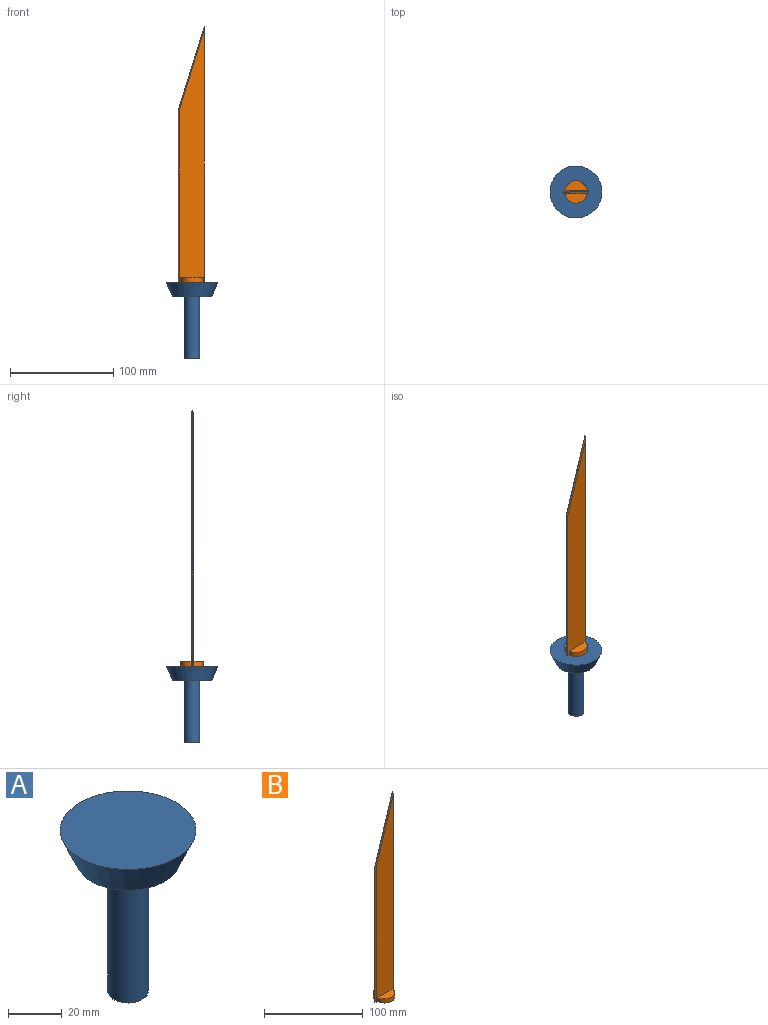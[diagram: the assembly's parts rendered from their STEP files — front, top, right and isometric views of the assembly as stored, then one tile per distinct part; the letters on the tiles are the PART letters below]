
ASSEMBLY  parts=2 mates=1
PART A: 5 faces, bbox 50.4x50.4x73.2 mm
  f0: plane 50.44x50.44mm, normal (0,0,1), area 1998.6mm2, adj f1
  f1: cone r=25.22mm half-angle=23.7deg, axis (0,0,1), area 2088mm2, adj f0,f2
  f2: plane 38.42x38.42mm, normal (0,0,-1), area 981.7mm2, adj f1,f3
  f3: cylinder r=7.52mm len=59.46mm, axis (0,0,1), area 2808.4mm2, adj f2,f4
  f4: plane 15.03x15.03mm, normal (0,0,-1), area 177.5mm2, adj f3
PART B: 13 faces, bbox 25.4x21.8x248.8 mm
  f0: plane 2.61x2mm, normal (0,0,-1), area 4.1mm2, adj f1,f2,f7,f8,f10
  f1: plane 245.33x24.4mm, normal (0,-1,0), area 4918.2mm2, adj f0,f3,f4,f5,f7,f10,f11
  f2: plane 245.33x24.4mm, normal (0,1,0), area 4917.6mm2, adj f0,f3,f4,f6,f8,f9,f10
  f3: plane 2x1.14mm, normal (0,0,-1), area 2.2mm2, adj f1,f2,f4,f10
  f4: plane 248.71x2mm, normal (1,0,0), area 494mm2, adj f1,f2,f3,f5,f6
  f5: plane 82.19x25.4mm, normal (-0.68,-0.71,0.21), area 119.1mm2, adj f1,f4,f6,f7
  f6: plane 82.19x25.4mm, normal (-0.68,0.71,0.21), area 119.1mm2, adj f2,f4,f5,f8
  f7: plane 166.66x1mm, normal (-0.71,-0.71,0), area 235.6mm2, adj f0,f1,f5,f8
  f8: plane 166.66x1mm, normal (-0.71,0.71,0), area 235.6mm2, adj f0,f2,f6,f7
  f9: plane 21.77x10.24mm, normal (0,0,1), area 172.3mm2, adj f2,f10
  f10: cylinder r=10.91mm len=21.81mm, axis (0,0,-1), area 323mm2, adj f0,f1,f2,f3,f9,f11,f12
  f11: plane 21.65x9.58mm, normal (0,0,1), area 157.9mm2, adj f1,f10
  f12: plane 21.81x21.81mm, normal (0,0,-1), area 373.8mm2, adj f10
PLACE A t=(93.8,114.69,15.5)mm
PLACE B t=(80.27,115.36,135.11)mm
MATE fastened B.f10 <-> A.f1  axis (0,0,-1) through (93.8,114.69,41.89)mm
